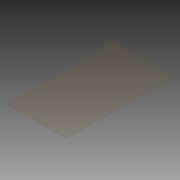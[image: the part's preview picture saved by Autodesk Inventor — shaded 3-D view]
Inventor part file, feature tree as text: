
AUTODESK INVENTOR PART (.ipt)
format: ipt  version: 2012 (Build 160160000, 160)  size: 65,536 bytes
history: native  units: in
note: dims shown in document units (in); Inventor stores cm internally (conversion verified against a paired STEP export)
features: extrude x1, sketch x1
ambient origin geometry x8: Origin, YZ Plane, XZ Plane, XY Plane, X Axis, Y Axis, Z Axis, Center Point
bodies: Solid1 (feature_tree)
feature tree (2):
  extrude  "Extrusion1"  Depth=11.25in
  sketch  "Sketch1"  dims[d0=0.125in d1=11.25in d2=20.0in d3=0.0in]
